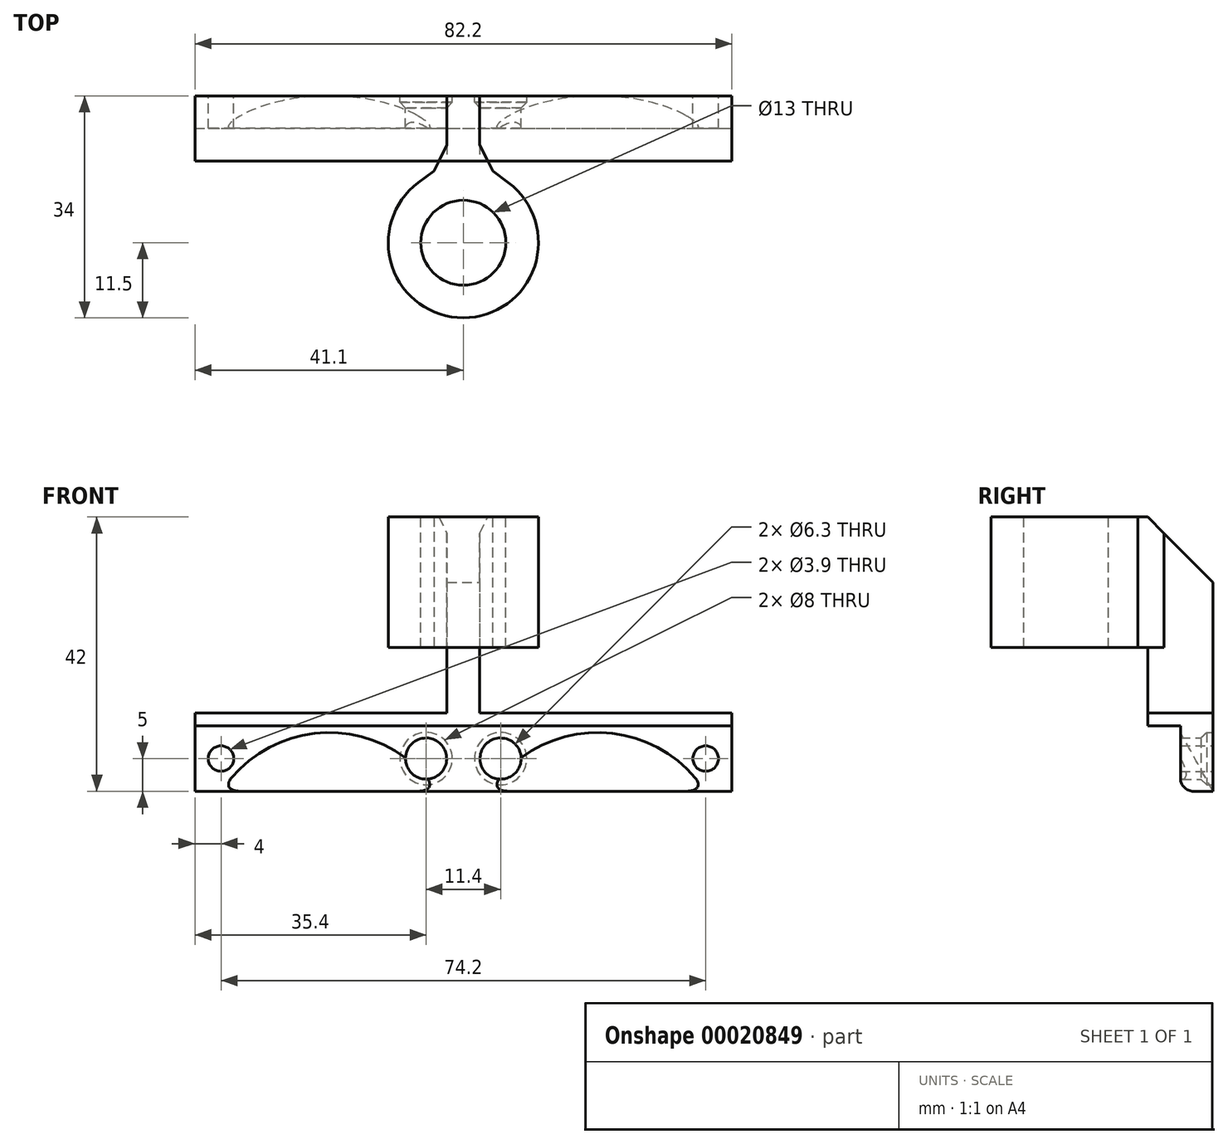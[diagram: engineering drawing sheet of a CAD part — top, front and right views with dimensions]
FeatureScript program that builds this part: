
annotation { "Feature Type Name" : "Feature", "Feature Type Description" : "" }
export const myFeature = defineFeature(function(context is Context, id is Id, definition is map)
    precondition{}
    {
        {
            var Q0;
            Q0=qCreatedBy(makeId("Front.planeOp"),FACE);
            var sketch = newSketch(context, id + "F0", { "sketchPlane" : qUnion([Q0])});
            skLineSegment(sketch, "E0.rect.bottom", {"start": v(-41.1, 5) * mm, "end": v(41.1, 5) * mm});
            skLineSegment(sketch, "E0.rect.top", {"start": v(-41.1, -5) * mm, "end": v(41.1, -5) * mm});
            skLineSegment(sketch, "E0.rect.left", {"start": v(-41.1, 5) * mm, "end": v(-41.1, -5) * mm});
            skLineSegment(sketch, "E0.rect.right", {"start": v(41.1, 5) * mm, "end": v(41.1, -5) * mm});
            skPoint(sketch, "E0.rect.middle", {"position": v(0, 0) * mm});
            skCircle(sketch, "E1", {"center": v(-37.1, 0) * mm, "radius": 1.95 * mm});
            skCircle(sketch, "E2.MirrorC", {"center": v(37.1, 0) * mm, "radius": 1.95 * mm});
            skSolve(sketch);
        }
        {
            var Q0;
            Q0=qSketchRegion(id+"F0",true);
            extrude(context, id + "F1", {"entities" : qUnion([Q0]), "depth" : 5 * mm});
        }
        {
            var Q0;
            Q0=makeQuery(id+"F1.opExtrude","CAP_FACE",FACE,{"disambiguationData":[OSD([sQuery(id+"F0.wireOp",EDGE,"E0.rect.bottom"),sQuery(id+"F0.wireOp",EDGE,"E0.rect.top"),sQuery(id+"F0.wireOp",EDGE,"E0.rect.left"),sQuery(id+"F0.wireOp",EDGE,"E0.rect.right"),sQuery(id+"F0.wireOp",EDGE,"E1"),sQuery(id+"F0.wireOp",EDGE,"E2.MirrorC")])],"isStart":false});
            var sketch = newSketch(context, id + "F2", { "sketchPlane" : qUnion([Q0])});
            skLineSegment(sketch, "E3", {"start": v(-41.1, 5) * mm, "end": v(0, 5) * mm, "construction": true});
            skPoint(sketch, "E4", {"position": v(-20.55, 5) * mm});
            skCircle(sketch, "E5", {"center": v(-20.55, -15.55) * mm, "radius": 19.55 * mm});
            skSolve(sketch);
        }
        {
            var Q0;
            Q0=qCreatedBy(makeId("Right.planeOp"),FACE);
            var Q1;
            Q1=sQuery(id+"F2.wireOp",VERTEX,"E4");
            cPlane(context, id + "F3", {"entities" : qUnion([Q0, Q1]), "cplaneType" : CPlaneType.PLANE_POINT, "offset" : 25 * mm, "width" : 150 * mm, "height" : 150 * mm});
        }
        {
            var Q0;
            Q0=qCreatedBy(id+"F3.planeOp",FACE);
            var sketch = newSketch(context, id + "F4", { "sketchPlane" : qUnion([Q0])});
            skLineSegment(sketch, "E6", {"start": v(-5, 4) * mm, "end": v(0, -5) * mm});
            skSolve(sketch);
        }
        {
            var Q0;
            Q0 = qSketchRegion(id + "F2", true);
            var Q1;
            Q1 = qConstructionFilter(qBodyType(qCreatedBy(id + "F4" ,EDGE), BodyType.WIRE), ConstructionObject.NO);
            sweep(context, id + "F5", {"profiles" : qUnion([Q0]), "path" : qUnion([Q1])});
        }
        {
            var Q0;
            Q0=makeQuery(id+"F5.opSweep","SWEPT_BODY",BODY,{"disambiguationData":[OSD([sQuery(id+"F2.wireOp",EDGE,"E5"),sQuery(id+"F4.wireOp",EDGE,"E6")])]});
            var Q1;
            Q1=qCreatedBy(makeId("Right.planeOp"),FACE);
            mirror(context, id + "F6", {"entities" : qUnion([Q0]), "mirrorPlane" : qUnion([Q1])});
        }
        {
            var Q0;
            Q0=makeQuery(id+"F5.opSweep","SWEPT_BODY",BODY,{"disambiguationData":[OSD([sQuery(id+"F2.wireOp",EDGE,"E5"),sQuery(id+"F4.wireOp",EDGE,"E6")])]});
            var Q1;
            Q1=makeQuery(id+"F6.opPattern","COPY",BODY,{"derivedFrom":makeQuery(id+"F5.opSweep","SWEPT_BODY",BODY,{"disambiguationData":[OSD([sQuery(id+"F2.wireOp",EDGE,"E5"),sQuery(id+"F4.wireOp",EDGE,"E6")])]}),"instanceName":"1"});
            var Q2;
            Q2=makeQuery(id+"F1.opExtrude","SWEPT_BODY",BODY,{"disambiguationData":[OSD([sQuery(id+"F0.wireOp",EDGE,"E0.rect.bottom"),sQuery(id+"F0.wireOp",EDGE,"E0.rect.top"),sQuery(id+"F0.wireOp",EDGE,"E0.rect.left"),sQuery(id+"F0.wireOp",EDGE,"E0.rect.right"),sQuery(id+"F0.wireOp",EDGE,"E1"),sQuery(id+"F0.wireOp",EDGE,"E2.MirrorC")])]});
            booleanBodies(context, id + "F7", {"operationType" : BooleanOperationType.SUBTRACTION, "tools" : qUnion([Q0, Q1]), "targets" : qUnion([Q2])});
        }
        {
            var Q0;
            Q0=makeQuery(id+"F1.opExtrude","CAP_FACE",FACE,{"disambiguationData":[OSD([sQuery(id+"F0.wireOp",EDGE,"E0.rect.bottom"),sQuery(id+"F0.wireOp",EDGE,"E0.rect.top"),sQuery(id+"F0.wireOp",EDGE,"E0.rect.left"),sQuery(id+"F0.wireOp",EDGE,"E0.rect.right"),sQuery(id+"F0.wireOp",EDGE,"E1"),sQuery(id+"F0.wireOp",EDGE,"E2.MirrorC")])],"isStart":true});
            var sketch = newSketch(context, id + "F8", { "sketchPlane" : qUnion([Q0])});
            skCircle(sketch, "E7", {"center": v(5.7, 0) * mm, "radius": 3.15 * mm});
            skCircle(sketch, "E8.MirrorC", {"center": v(-5.7, 0) * mm, "radius": 3.15 * mm});
            skSolve(sketch);
        }
        {
            var Q0;
            Q0=qSketchRegion(id+"F8",true);
            extrude(context, id + "F9", {"entities" : qUnion([Q0]), "operationType" : NewBodyOperationType.REMOVE, "endBound" : BoundingType.THROUGH_ALL, "oppositeDirection" : true, "depth" : 4 * mm});
        }
        {
            var Q0;
            Q0=makeQuery(id+"F1.opExtrude","CAP_FACE",FACE,{"disambiguationData":[OSD([sQuery(id+"F0.wireOp",EDGE,"E0.rect.bottom"),sQuery(id+"F0.wireOp",EDGE,"E0.rect.top"),sQuery(id+"F0.wireOp",EDGE,"E0.rect.left"),sQuery(id+"F0.wireOp",EDGE,"E0.rect.right"),sQuery(id+"F0.wireOp",EDGE,"E1"),sQuery(id+"F0.wireOp",EDGE,"E2.MirrorC")])],"isStart":true});
            var sketch = newSketch(context, id + "F10", { "sketchPlane" : qUnion([Q0])});
            skCircle(sketch, "E9", {"center": v(5.7, 0) * mm, "radius": 4 * mm});
            skCircle(sketch, "E10.MirrorC", {"center": v(-5.7, 0) * mm, "radius": 4 * mm});
            skSolve(sketch);
        }
        {
            var Q0;
            Q0=qSketchRegion(id+"F10",true);
            extrude(context, id + "F11", {"entities" : qUnion([Q0]), "operationType" : NewBodyOperationType.REMOVE, "oppositeDirection" : true, "depth" : 2 * mm});
        }
        {
            var Q0;
            Q0=makeQuery(id+"F11.boolean.opBoolean","COPY",EDGE,{"derivedFrom":makeQuery(id+"F11.opExtrude","CAP_EDGE",EDGE,{"disambiguationData":[OSD([sQuery(id+"F10.wireOp",EDGE,"E10.MirrorC")])],"isStart":false})});
            var Q1;
            Q1=makeQuery(id+"F11.boolean.opBoolean","COPY",EDGE,{"derivedFrom":makeQuery(id+"F11.opExtrude","CAP_EDGE",EDGE,{"disambiguationData":[OSD([sQuery(id+"F10.wireOp",EDGE,"E9")])],"isStart":false})});
            chamfer(context, id + "F12", {"entities" : qUnion([Q0, Q1]), "width" : 1 * mm, "tangentPropagation" : true});
        }
        {
            var Q0;
            Q0=makeQuery(id+"F1.opExtrude","SWEPT_FACE",FACE,{"disambiguationData":[OSD([sQuery(id+"F0.wireOp",EDGE,"E0.rect.bottom")])]});
            var sketch = newSketch(context, id + "F13", { "sketchPlane" : qUnion([Q0])});
            skLineSegment(sketch, "E11.bottom", {"start": v(41.1, 0) * mm, "end": v(-41.1, 0) * mm});
            skLineSegment(sketch, "E11.top", {"start": v(41.1, -10) * mm, "end": v(-41.1, -10) * mm});
            skLineSegment(sketch, "E11.left", {"start": v(41.1, 0) * mm, "end": v(41.1, -10) * mm});
            skLineSegment(sketch, "E11.right", {"start": v(-41.1, 0) * mm, "end": v(-41.1, -10) * mm});
            skSolve(sketch);
        }
        {
            var Q0;
            Q0=qSketchRegion(id+"F13",true);
            extrude(context, id + "F14", {"entities" : qUnion([Q0]), "operationType" : NewBodyOperationType.ADD, "depth" : 2 * mm});
        }
        {
            var Q0;
            Q0=makeQuery(id+"F14.opExtrude","CAP_FACE",FACE,{"disambiguationData":[OSD([sQuery(id+"F13.wireOp",EDGE,"E11.bottom"),sQuery(id+"F13.wireOp",EDGE,"E11.top"),sQuery(id+"F13.wireOp",EDGE,"E11.left"),sQuery(id+"F13.wireOp",EDGE,"E11.right")])],"isStart":false});
            var sketch = newSketch(context, id + "F15", { "sketchPlane" : qUnion([Q0])});
            skLineSegment(sketch, "E12.rect.bottom", {"start": v(-2.5, 0) * mm, "end": v(2.5, 0) * mm});
            skLineSegment(sketch, "E12.rect.top", {"start": v(-2.5, -10) * mm, "end": v(2.5, -10) * mm});
            skLineSegment(sketch, "E12.rect.left", {"start": v(-2.5, 0) * mm, "end": v(-2.5, -10) * mm});
            skLineSegment(sketch, "E12.rect.right", {"start": v(2.5, 0) * mm, "end": v(2.5, -10) * mm});
            skPoint(sketch, "E12.rect.middle", {"position": v(0, -5) * mm});
            skPoint(sketch, "E12.rect.middle.positionSnap0", {"position": v(-41.1, -5) * mm});
            skPoint(sketch, "E12.rect.centerSnap0", {"position": v(-41.1, -5) * mm});
            skSolve(sketch);
        }
        {
            var Q0;
            Q0 = qSketchRegion(id + "F15", true);
            extrude(context, id + "F16", {"entities" : qUnion([Q0]), "operationType" : NewBodyOperationType.ADD, "depth" : 30 * mm});
        }
        {
            var Q0;
            Q0=makeQuery(id+"F16.opExtrude","CAP_FACE",FACE,{"disambiguationData":[OSD([sQuery(id+"F15.wireOp",EDGE,"E12.rect.bottom"),sQuery(id+"F15.wireOp",EDGE,"E12.rect.top"),sQuery(id+"F15.wireOp",EDGE,"E12.rect.left"),sQuery(id+"F15.wireOp",EDGE,"E12.rect.right")])],"isStart":false});
            var sketch = newSketch(context, id + "F17", { "sketchPlane" : qUnion([Q0])});
            skCircle(sketch, "E13", {"center": v(0, -22.5) * mm, "radius": 6.5 * mm});
            skArc(sketch, "E14", {"start": v(-6.9, -13.3) * mm, "mid": v(0, -34) * mm, "end": v(6.9, -13.3) * mm});
            skLineSegment(sketch, "E15", {"start": v(2.5, -10) * mm, "end": v(6.9, -13.3) * mm});
            skLineSegment(sketch, "E16", {"start": v(2.5, -10) * mm, "end": v(0, -10) * mm});
            skLineSegment(sketch, "E17.MirrorCS", {"start": v(-2.5, -10) * mm, "end": v(-6.9, -13.3) * mm});
            skLineSegment(sketch, "E18.MirrorCS", {"start": v(-2.5, -10) * mm, "end": v(0, -10) * mm});
            skSolve(sketch);
        }
        {
            var Q0;
            Q0 = qSketchRegion(id + "F17", true);
            extrude(context, id + "F18", {"entities" : qUnion([Q0]), "operationType" : NewBodyOperationType.ADD, "oppositeDirection" : true, "depth" : 20 * mm});
        }
        {
            var Q0;
            Q0=makeQuery(id+"F1.opExtrude","CAP_EDGE",EDGE,{"disambiguationData":[OSD([sQuery(id+"F0.wireOp",EDGE,"E0.rect.top")])],"isStart":false});
            fillet(context, id + "F19", {"entities" : qUnion([Q0]), "radius" : 2 * mm, "tangentPropagation" : true, "allowEdgeOverflow" : false});
        }
        {
            var Q0;
            {var subQ0=sQuery(id+"F15.wireOp",EDGE,"E12.rect.right");Q0=makeQuery(id+"F18.boolean.opBoolean","MERGE",EDGE,{"derivedFrom":[makeQuery(id+"F16.opExtrude","SWEPT_EDGE",EDGE,{"disambiguationData":[OSD([sQuery(id+"F13.wireOp",EDGE,"E11.top"),sQuery(id+"F15.wireOp",EDGE,"E12.rect.top"),subQ0])]}),makeQuery(id+"F18.opExtrude","SWEPT_EDGE",EDGE,{"disambiguationData":[OSD([subQ0,sQuery(id+"F17.wireOp",EDGE,"E15"),sQuery(id+"F17.wireOp",EDGE,"E16")])]})]});}
            var Q1;
            {var subQ0=sQuery(id+"F15.wireOp",EDGE,"E12.rect.left");Q1=makeQuery(id+"F18.boolean.opBoolean","MERGE",EDGE,{"derivedFrom":[makeQuery(id+"F16.opExtrude","SWEPT_EDGE",EDGE,{"disambiguationData":[OSD([sQuery(id+"F13.wireOp",EDGE,"E11.top"),sQuery(id+"F15.wireOp",EDGE,"E12.rect.top"),subQ0])]}),makeQuery(id+"F18.opExtrude","SWEPT_EDGE",EDGE,{"disambiguationData":[OSD([subQ0,sQuery(id+"F17.wireOp",EDGE,"E17.MirrorCS"),sQuery(id+"F17.wireOp",EDGE,"E18.MirrorCS")])]})]});}
            chamfer(context, id + "F20", {"entities" : qUnion([Q0, Q1]), "width" : 5 * mm, "tangentPropagation" : true});
        }
        {
            var Q0;
            Q0=makeQuery(id+"F16.opExtrude","CAP_EDGE",EDGE,{"disambiguationData":[OSD([sQuery(id+"F15.wireOp",EDGE,"E12.rect.bottom")])],"isStart":false});
            chamfer(context, id + "F21", {"entities" : qUnion([Q0]), "width" : 10 * mm, "tangentPropagation" : true});
        }
    });
